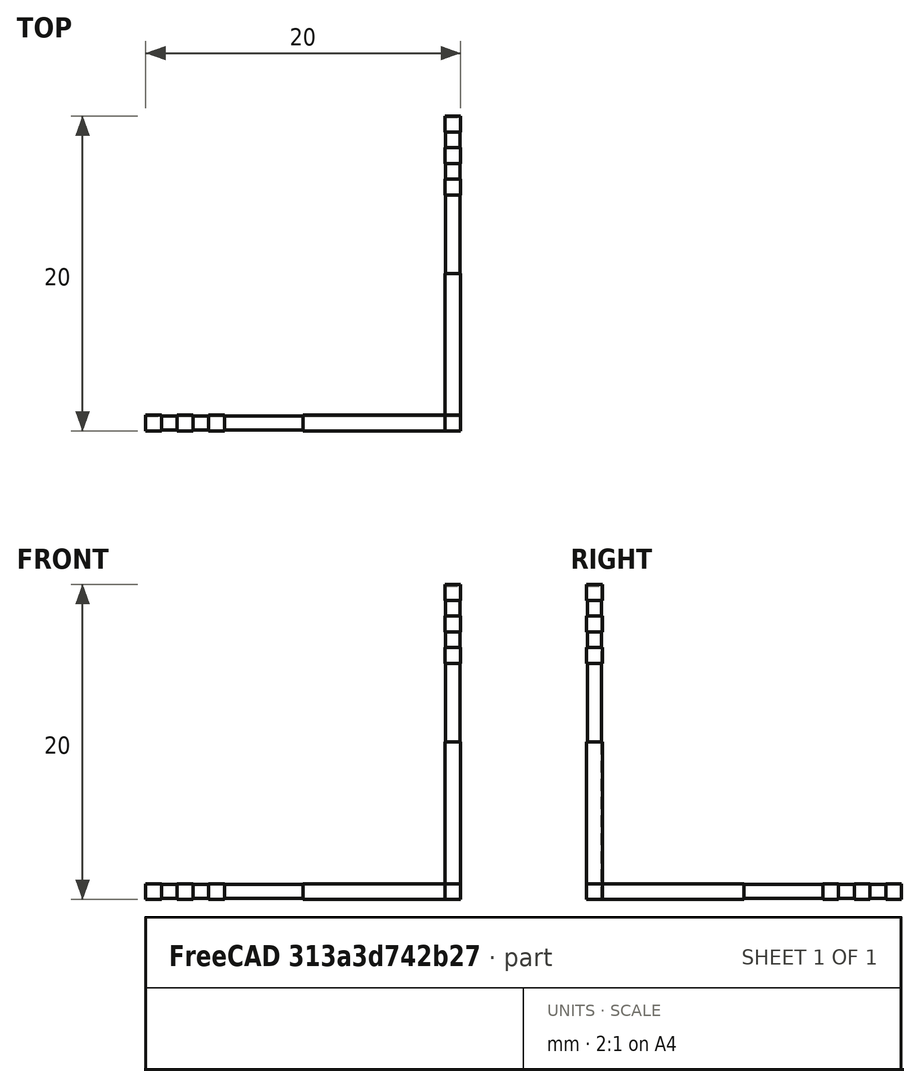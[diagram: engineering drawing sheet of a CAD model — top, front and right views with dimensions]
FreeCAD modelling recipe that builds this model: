
FCSTD DOCUMENT  (FreeCAD 0.19R24344 (Git))
Label: Scale Bar
License: Creative Commons Attribution-NonCommercial-ShareAlike
LicenseURL: http://creativecommons.org/licenses/by-nc-sa/4.0/
objects: Part::Box×15, Part::Part2DObjectPython×2, PartDesign::CoordinateSystem×1, App::Part×1
note: 18 computed .brp shape members not serialized (recipe doc carries the construction recipe); baked Part::Feature solids carry a one-line shape summary decoded from their .brp

FEATURE [Part::Box] Box  label="Cube"
  AttacherType = Attacher::AttachEngine3D
  Height = 1
  Length = 10
  Placement = pos=(-10,0,0) rot=(0,0,1;0rad)
  Width = 1
FEATURE [Part::Box] Box001  label="Cube001"
  AttacherType = Attacher::AttachEngine3D
  Height = 1
  Length = 1
  Placement = pos=(-16,0,0) rot=(0,0,1;0rad)
  Width = 1
FEATURE [Part::Box] Box002  label="Cube002"
  AttacherType = Attacher::AttachEngine3D
  Height = 1
  Length = 1
  Placement = pos=(-18,0,0) rot=(0,0,1;0rad)
  Width = 1
FEATURE [Part::Box] Box003  label="Cube003"
  AttacherType = Attacher::AttachEngine3D
  Height = 1
  Length = 1
  Placement = pos=(-20,0,0) rot=(0,0,1;0rad)
  Width = 1
FEATURE [PartDesign::CoordinateSystem] LCS_0
  AttacherType = Attacher::AttachEngine3D
  MapMode = 2
  Support = -> [X_Axis]
FEATURE [Part::Box] Box004  label="Cube004"
  AttacherType = Attacher::AttachEngine3D
  Height = 1
  Length = 10
  Placement = pos=(-1,10,0) rot=(0,0,-1;1.5708rad)
  Width = 1
FEATURE [Part::Box] Box005  label="Cube005"
  AttacherType = Attacher::AttachEngine3D
  Height = 1
  Length = 1
  Placement = pos=(-1,16,0) rot=(0,0,-1;1.5708rad)
  Width = 1
FEATURE [Part::Box] Box006  label="Cube006"
  AttacherType = Attacher::AttachEngine3D
  Height = 1
  Length = 1
  Placement = pos=(-1,18,0) rot=(0,0,-1;1.5708rad)
  Width = 1
FEATURE [Part::Box] Box007  label="Cube007"
  AttacherType = Attacher::AttachEngine3D
  Height = 1
  Length = 1
  Placement = pos=(-1,20,0) rot=(0,0,-1;1.5708rad)
  Width = 1
FEATURE [Part::Box] Box010  label="Cube010"
  AttacherType = Attacher::AttachEngine3D
  Height = 1
  Length = 1
  Placement = pos=(-1,0,18) rot=(0,1,0;1.5708rad)
  Width = 1
FEATURE [Part::Box] Box008  label="Cube008"
  AttacherType = Attacher::AttachEngine3D
  Height = 1
  Length = 10
  Placement = pos=(-1,0,10) rot=(0,1,0;1.5708rad)
  Width = 1
FEATURE [Part::Box] Box009  label="Cube009"
  AttacherType = Attacher::AttachEngine3D
  Height = 1
  Length = 1
  Placement = pos=(-1,0,16) rot=(0,1,0;1.5708rad)
  Width = 1
FEATURE [Part::Box] Box011  label="Cube011"
  AttacherType = Attacher::AttachEngine3D
  Height = 1
  Length = 1
  Placement = pos=(-1,0,20) rot=(0,1,0;1.5708rad)
  Width = 1
FEATURE [Part::Box] Box012  label="Cube012"
  AttacherType = Attacher::AttachEngine3D
  Height = 19.9
  Length = 0.9
  Placement = pos=(-0.95,0.05,0) rot=(0,0,1;0rad)
  Width = 0.9
FEATURE [Part::Box] Box013  label="Cube013"
  AttacherType = Attacher::AttachEngine3D
  Height = 0.9
  Length = 19.9
  Placement = pos=(-19.95,0.05,0.05) rot=(0,0,1;0rad)
  Width = 0.9
FEATURE [Part::Box] Box014  label="Cube014"
  AttacherType = Attacher::AttachEngine3D
  Height = 0.9
  Length = 0.9
  Placement = pos=(-0.95,0.05,0.05) rot=(0,0,1;0rad)
  Width = 19.9
FEATURE [Part::Part2DObjectPython] ShapeString  label="X-Label"  # Draft 2D object (typed FeaturePython)
  FontFile = <userpath>/prj/2019_Janelia_Component-Design/Extra/Scale Bar/DejaVuSans.ttf
  Placement = pos=(-18.94,2,0) rot=(0,0,1;0rad)
  Size = 4
  String = 20mm
  Tracking = 0
FEATURE [Part::Part2DObjectPython] ShapeString001  label="Y-Label"  # Draft 2D object (typed FeaturePython)
  FontFile = <userpath>/prj/2019_Janelia_Component-Design/Extra/Scale Bar/DejaVuSans.ttf
  Placement = pos=(0,2,2) rot=(0,1,0;36.1283rad)
  Size = 4
  String = 20mm
  Tracking = 0
FEATURE [App::Part] Scalebar
  Group = -> [LCS_0,Box,Box001,Box002,Box003,Box004,Box005,Box006,Box007,Box008,Box009,Box010,Box011,Box012,Box013,Box014,ShapeString,ShapeString001]
  Origin = -> Origin
